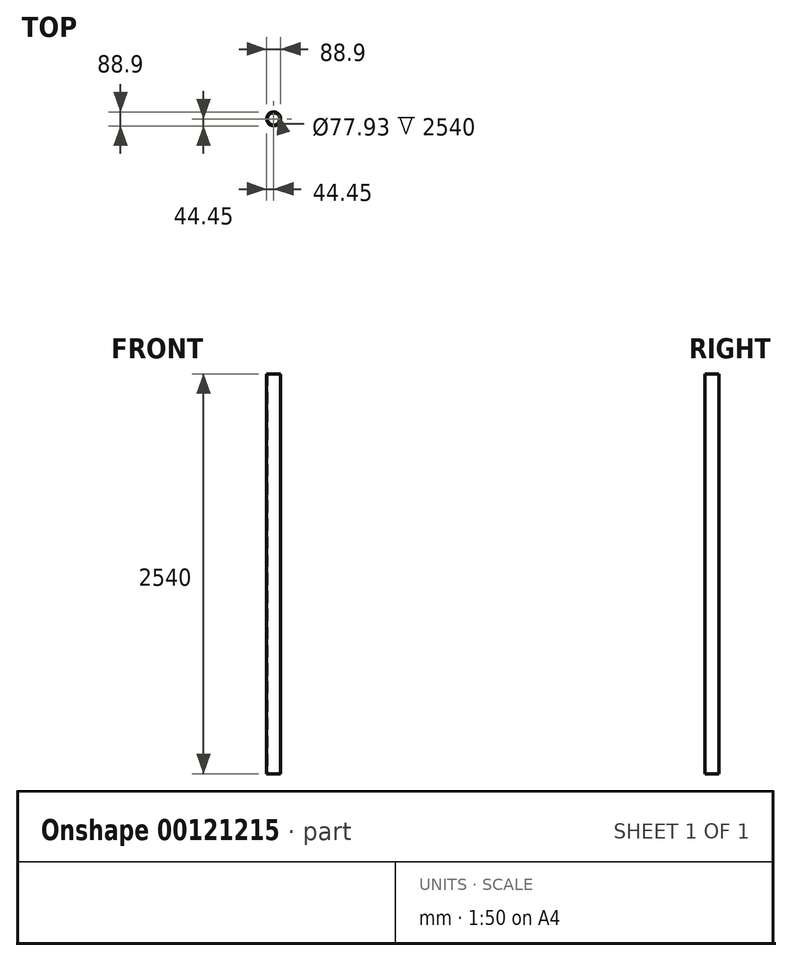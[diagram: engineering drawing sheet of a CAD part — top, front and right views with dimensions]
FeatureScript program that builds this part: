
annotation { "Feature Type Name" : "Feature", "Feature Type Description" : "" }
export const myFeature = defineFeature(function(context is Context, id is Id, definition is map)
    precondition{}
    {
        {
            var Q0;
            Q0=qCreatedBy(makeId("Top.planeOp"),FACE);
            var sketch = newSketch(context, id + "F0", { "sketchPlane" : qUnion([Q0])});
            skCircle(sketch, "E0", {"center": v(0, 0) * mm, "radius": 44.45 * mm});
            skCircle(sketch, "E1", {"center": v(0, 0) * mm, "radius": 38.96 * mm});
            skSolve(sketch);
        }
        {
            var Q0;
            Q0 = qSketchRegion(id + "F0", true);
            extrude(context, id + "F1", {"entities" : qUnion([Q0]), "depth" : 2540 * mm});
        }
    });
